# Revit family: Haworth_Planes_HeightAdjustTable_Corner120
name_source: partatom
category: Furniture Systems
units: mm (PartAtom-declared; Revit-internal decimal feet)

## family parameters
Always vertical = Yes
Cut with Voids When Loaded = No
OmniClass Number = 23.40.70.14.64.21
OmniClass Title = Systems Furniture
Part Type = Normal
Room Calculation Point = No
Round Connector Dimension = Use Diameter
Shared = No
Work Plane-Based = No

## types (4) — shared parameters
Assembly Code = E2020200
Custom Size = No
Leg Trim Finish = Haworth _ Paint _ Black
Manufacturer = Haworth
Max. Depth = 29"
Max. Height = 46"
Max. Width = 58"
Min. Depth = 23"
Min. Height = 27"
Min. Width = 52"
Min/Max Depth = 23 or 29 in.
Min/Max Width/Length = 52 or 58 in.
Model = TACZ
Revision Number = 2
Size = Verify Final Dim. w/ Haworth
Sustainability Info = https://www.haworth.com
Table Thickness = 1 3/16"
URL = www.haworth.com
URL - Product = http://www.haworth.com
Warranty = http://www.haworth.com

## per-type parameters (varying)
| type | Actual Depth | Actual Width | Base Tube Finish | Crank Adjustment | Depth | Description | Leg Back Offset | Leg Depth 23 | Leg Depth 29 | Leg Side Offset | Width |
| 58w 29d | 29" | 58" | Haworth _ Paint _ Undecided _ Table | No | 29" | Haworth - Planes HAT Corner 120 - 58w 29d | 9 3/32" | No | Yes | 3 1/4" | 58" |
| 58w 23d | 23" | 58" | Haworth _ Paint _ Smoke | Yes | 23" | Haworth - Planes HAT Corner 120 - 58w 23d | 6 1/2" | Yes | No | 6 1/4" | 58" |
| 52w 29d | 29" | 52" | Haworth _ Paint _ Smoke | Yes | 29" | Haworth - Planes HAT Corner 120 - 52w 29d | 9 3/32" | No | Yes | 3 1/4" | 52" |
| 52w 23d | 23" | 52" | Haworth _ Paint _ Smoke | Yes | 23" | Haworth - Planes HAT Corner 120 - 52w 23d | 6 1/2" | Yes | No | 6 1/4" | 52" |

## geometry (parser evidence)
native form markers: Sweep x10
no freeform markers — native parametric forms only
